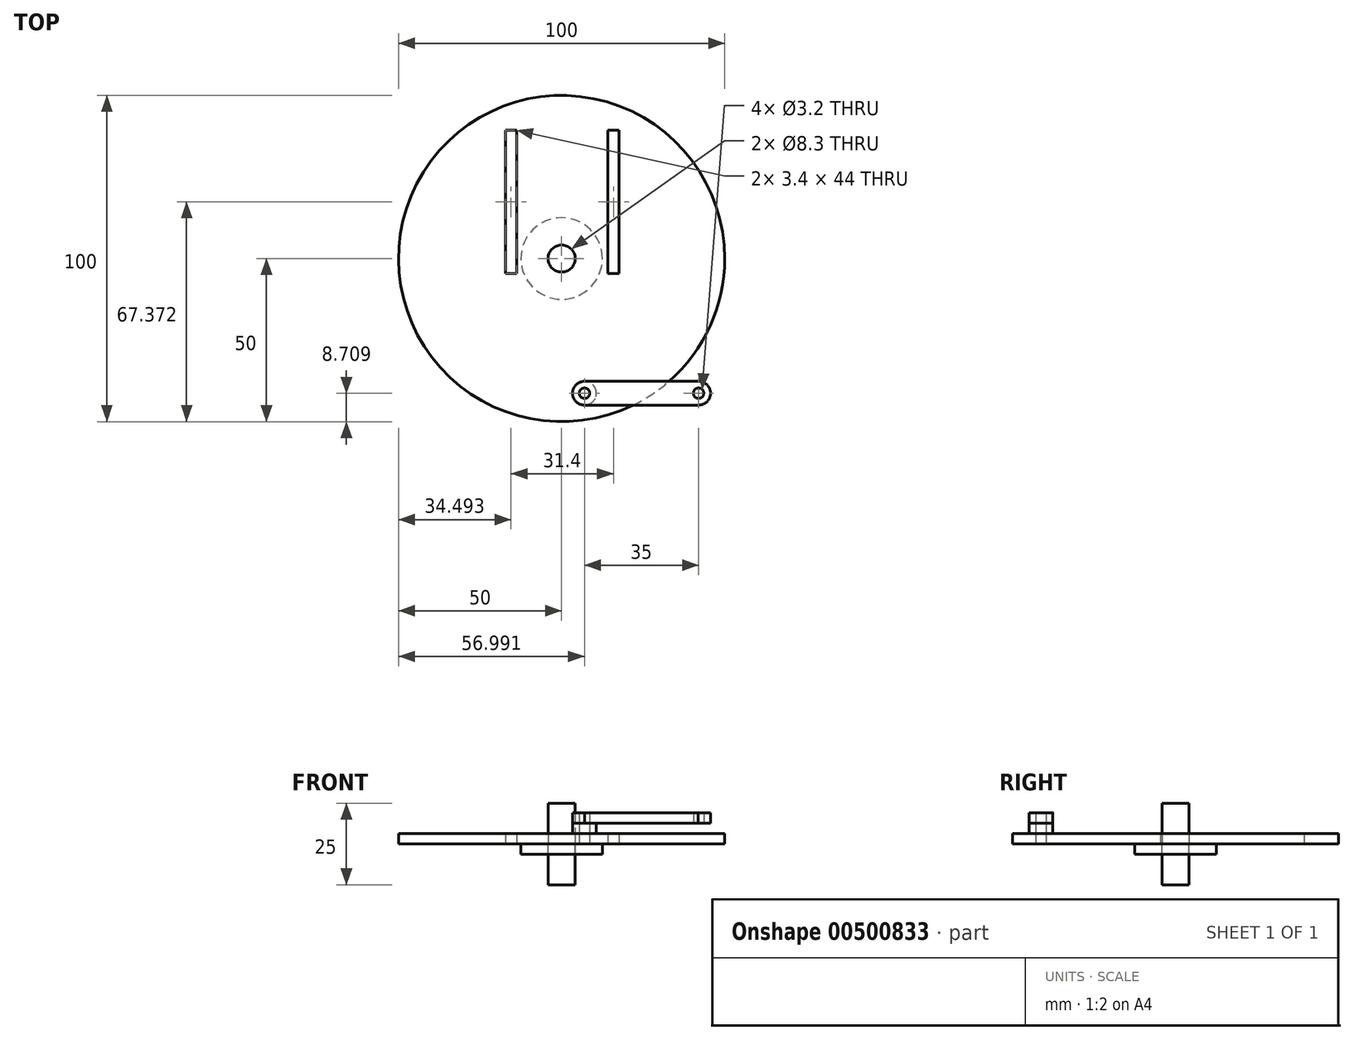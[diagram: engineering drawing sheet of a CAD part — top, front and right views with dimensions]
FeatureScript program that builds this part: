
annotation { "Feature Type Name" : "Feature", "Feature Type Description" : "" }
export const myFeature = defineFeature(function(context is Context, id is Id, definition is map)
    precondition{}
    {
        {
            var Q0;
            Q0=qCreatedBy(makeId("Top.planeOp"),FACE);
            var sketch = newSketch(context, id + "F0", { "sketchPlane" : qUnion([Q0])});
            skCircle(sketch, "E0", {"center": v(0, 0) * mm, "radius": 50 * mm});
            skCircle(sketch, "E1", {"center": v(7, -41.3) * mm, "radius": 1.6 * mm});
            skCircle(sketch, "E2", {"center": v(0, 0) * mm, "radius": 4.15 * mm});
            skLineSegment(sketch, "E3.bottom", {"start": v(-17.2, 39.37) * mm, "end": v(-13.8, 39.37) * mm});
            skLineSegment(sketch, "E3.top", {"start": v(-17.2, -4.63) * mm, "end": v(-13.8, -4.63) * mm});
            skLineSegment(sketch, "E3.left", {"start": v(-17.2, 39.37) * mm, "end": v(-17.2, -4.63) * mm});
            skLineSegment(sketch, "E3.right", {"start": v(-13.8, 39.37) * mm, "end": v(-13.8, -4.63) * mm});
            skLineSegment(sketch, "E4.left", {"start": v(14.2, 39.37) * mm, "end": v(14.2, -4.63) * mm});
            skLineSegment(sketch, "E4.right", {"start": v(17.6, 39.37) * mm, "end": v(17.6, -4.63) * mm});
            skLineSegment(sketch, "E5", {"start": v(14.2, 39.37) * mm, "end": v(17.6, 39.37) * mm});
            skLineSegment(sketch, "E6", {"start": v(17.6, -4.63) * mm, "end": v(14.2, -4.63) * mm});
            skSolve(sketch);
        }
        {
            var Q0;
            Q0 = qSketchRegion(id + "F0", true);
            extrude(context, id + "F1", {"entities" : qUnion([Q0]), "depth" : 3.2 * mm, "offsetDistance" : 25 * mm});
        }
        {
            var Q0;
            Q0=makeQuery(id+"F0.imprint","IMPRINT",FACE,{"disambiguationData":[TD([[makeQuery(id+"F0.imprint","IMPRINT",EDGE,{"derivedFrom":sQuery(id+"F0.wireOp",EDGE,"E0")}),1.0]])]});
            var sketch = newSketch(context, id + "F2", { "sketchPlane" : qUnion([Q0])});
            skCircle(sketch, "E7", {"center": v(0, 0) * mm, "radius": 12.5 * mm});
            skSolve(sketch);
        }
        {
            var Q0;
            Q0=makeQuery(id+"F2.imprint","IMPRINT",FACE,{"disambiguationData":[TD([[makeQuery(id+"F2.imprint","IMPRINT",EDGE,{"derivedFrom":sQuery(id+"F2.wireOp",EDGE,"E7")}),1.0]])]});
            extrude(context, id + "F3", {"entities" : qUnion([Q0]), "oppositeDirection" : true, "depth" : 3.2 * mm, "offsetDistance" : 25 * mm});
        }
        {
            var Q0;
            Q0=makeQuery(id+"F0.imprint","IMPRINT",FACE,{"disambiguationData":[TD([[makeQuery(id+"F0.imprint","IMPRINT",EDGE,{"derivedFrom":sQuery(id+"F0.wireOp",EDGE,"E2")}),1.0]])]});
            var Q1;
            Q1=sQuery(id+"F0.wireOp",EDGE,"E2");
            extrude(context, id + "F4", {"entities" : qUnion([Q0]), "surfaceEntities" : qUnion([Q1]), "depth" : 25 * mm, "offsetDistance" : 25 * mm, "symmetric" : true});
        }
        {
            var Q0;
            Q0=makeQuery(id+"F1.opExtrude","CAP_FACE",FACE,{"disambiguationData":[OSD([sQuery(id+"F0.wireOp",EDGE,"E0"),sQuery(id+"F0.wireOp",EDGE,"E1"),sQuery(id+"F0.wireOp",EDGE,"E2"),sQuery(id+"F0.wireOp",EDGE,"E3.bottom"),sQuery(id+"F0.wireOp",EDGE,"E3.top"),sQuery(id+"F0.wireOp",EDGE,"E3.left"),sQuery(id+"F0.wireOp",EDGE,"E3.right"),sQuery(id+"F0.wireOp",EDGE,"E4.left"),sQuery(id+"F0.wireOp",EDGE,"E4.right"),sQuery(id+"F0.wireOp",EDGE,"E5"),sQuery(id+"F0.wireOp",EDGE,"E6")])],"isStart":false});
            var sketch = newSketch(context, id + "F5", { "sketchPlane" : qUnion([Q0])});
            skCircle(sketch, "E8", {"center": v(7, -41.3) * mm, "radius": 3.65 * mm});
            skSolve(sketch);
        }
        {
            var Q0;
            Q0=makeQuery(id+"F5.imprint","IMPRINT",FACE,{"disambiguationData":[TD([[makeQuery(id+"F5.imprint","IMPRINT",EDGE,{"derivedFrom":sQuery(id+"F5.wireOp",EDGE,"E8")}),1.0]])]});
            extrude(context, id + "F6", {"entities" : qUnion([Q0]), "depth" : 3.2 * mm, "offsetDistance" : 25 * mm});
        }
        {
            var Q0;
            Q0=makeQuery(id+"F6.opExtrude","CAP_FACE",FACE,{"disambiguationData":[OSD([sQuery(id+"F0.wireOp",EDGE,"E1"),sQuery(id+"F5.wireOp",EDGE,"E8")])],"isStart":false});
            var sketch = newSketch(context, id + "F7", { "sketchPlane" : qUnion([Q0])});
            skLineSegment(sketch, "E9", {"start": v(7, -44.94) * mm, "end": v(42, -44.94) * mm});
            skLineSegment(sketch, "E10", {"start": v(7, -37.64) * mm, "end": v(42, -37.64) * mm});
            skCircle(sketch, "E11", {"center": v(7, -41.3) * mm, "radius": 1.6 * mm});
            skCircle(sketch, "E12", {"center": v(7, -41.3) * mm, "radius": 3.65 * mm});
            skCircle(sketch, "E13", {"center": v(42, -41.3) * mm, "radius": 1.6 * mm});
            skCircle(sketch, "E14", {"center": v(42, -41.3) * mm, "radius": 3.65 * mm});
            skSolve(sketch);
        }
        {
            var Q0;
            Q0 = qSketchRegion(id + "F7", true);
            extrude(context, id + "F8", {"entities" : qUnion([Q0]), "depth" : 3.2 * mm, "offsetDistance" : 25 * mm});
        }
    });
